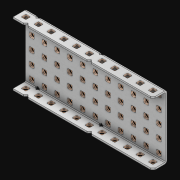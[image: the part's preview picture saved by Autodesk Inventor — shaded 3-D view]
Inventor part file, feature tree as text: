
AUTODESK INVENTOR PART (.ipt)
format: ipt  version: 2021 (Build 250183000, 183)  size: 3,133,440 bytes
history: native  units: in
note: dims shown in document units (in); Inventor stores cm internally (conversion verified against a paired STEP export)
features: extrude x78, other x77, sketch x4, thicken_offset x3, pattern_linear x3, imported_body x1
ambient origin geometry x8: Origin, YZ Plane, XZ Plane, XY Plane, X Axis, Y Axis, Z Axis, Center Point
bodies: Solid1 (feature_tree)
feature tree (166):
  thicken_offset  "Thicken1"
  thicken_offset  "Thicken2"
  thicken_offset  "Thicken3"
  pattern_linear  "Rectangular Pattern1"  Spacing1=0.001in  [1 undecoded]
  pattern_linear  "Rectangular Pattern2"  Spacing1=0.001in  [1 undecoded]
  pattern_linear  "Rectangular Pattern3"  Spacing1=0.182in  [1 undecoded]
  extrude  "Extrusion1"  Depth=0.063in TaperAngle=0.0deg
  sketch  "Sketch1"  dims[d0=0.001in]
  other  "Srf1"
  sketch  "Sketch2"  dims[d1=0.001in]
  other  "Srf2"
  sketch  "Sketch3"  dims[d2=0.001in]
  other  "Srf3"
  other  "Srf4"
  other  "Srf5"
  other  "Srf6"
  other  "Srf7"
  other  "Srf8"
  other  "Srf9"
  other  "Srf10"
  other  "Srf11"
  other  "Srf12"
  other  "Srf13"
  other  "Srf38"
  other  "Srf39"
  other  "Srf40"
  other  "Srf41"
  other  "Srf42"
  other  "Srf43"
  other  "Srf44"
  other  "Srf45"
  other  "Srf46"
  other  "Srf47"
  other  "Srf72"
  other  "Srf73"
  other  "Srf74"
  other  "Srf75"
  other  "Srf76"
  other  "Srf77"
  other  "Srf78"
  other  "Srf79"
  other  "Srf80"
  other  "Srf81"
  other  "Srf106"
  other  "Srf107"
  other  "Srf108"
  other  "Srf109"
  other  "Srf110"
  other  "Srf111"
  other  "Srf112"
  other  "Srf113"
  other  "Srf114"
  other  "Srf115"
  other  "Srf116"
  other  "Srf141"
  other  "Srf142"
  other  "Srf143"
  other  "Srf144"
  other  "Srf145"
  other  "Srf146"
  other  "Srf147"
  other  "Srf148"
  other  "Srf149"
  other  "Srf150"
  other  "Srf151"
  other  "Srf176"
  other  "Srf177"
  other  "Srf178"
  other  "Srf179"
  other  "Srf180"
  other  "Srf181"
  other  "Srf182"
  other  "Srf183"
  other  "Srf184"
  other  "Srf185"
  other  "Srf186"
  other  "Srf211"
  other  "Srf212"
  other  "Srf213"
  other  "Srf214"
  other  "Srf215"
  other  "Srf216"
  other  "Srf217"
  other  "Srf218"
  other  "Srf219"
  other  "Srf220"
  other  "Srf221"
  sketch  "Sketch4"  dims[d3=0.001in d4=0.001in d5=0.001in d6=0.182in d7=0.063in d8=0.0in d9=0.182in d10=0.063in d11=0.0in d12=0.182in d13=0.063in d14=0.0in d17=0.5in d18=4.3307in d20=0.5in d21=4.3307in d23=0.5in d24=1.9685in d26=0.5in d27=12.0in d28=0.0in]
  imported_body  "Imported1"
  extrude  "ExtrusionSrf1"  Depth=0.063in
  extrude  "ExtrusionSrf2"  Depth=0.063in TaperAngle=0.0deg
  extrude  "ExtrusionSrf3"  Depth=0.063in
  extrude  "ExtrusionSrf4"  Depth=0.063in TaperAngle=0.0deg
  extrude  "ExtrusionSrf5"  Depth=0.063in
  extrude  "ExtrusionSrf6"  Depth=0.063in
  extrude  "ExtrusionSrf7"  Depth=0.063in
  extrude  "ExtrusionSrf8"  Depth=0.063in
  extrude  "ExtrusionSrf9"  Depth=0.063in
  extrude  "ExtrusionSrf10"  Depth=0.063in
  extrude  "ExtrusionSrf11"  Depth=0.063in
  extrude  "ExtrusionSrf12"  TaperAngle=0.0deg  [1 undecoded]
  extrude  "ExtrusionSrf13"  [1 undecoded]
  extrude  "ExtrusionSrf38"  [1 undecoded]
  extrude  "ExtrusionSrf39"  [1 undecoded]
  extrude  "ExtrusionSrf40"  [1 undecoded]
  extrude  "ExtrusionSrf41"  [1 undecoded]
  extrude  "ExtrusionSrf42"  [1 undecoded]
  extrude  "ExtrusionSrf43"  [1 undecoded]
  extrude  "ExtrusionSrf44"  [1 undecoded]
  extrude  "ExtrusionSrf45"  [1 undecoded]
  extrude  "ExtrusionSrf46"  [1 undecoded]
  extrude  "ExtrusionSrf47"  [1 undecoded]
  extrude  "ExtrusionSrf72"  [1 undecoded]
  extrude  "ExtrusionSrf73"  [1 undecoded]
  extrude  "ExtrusionSrf74"  [1 undecoded]
  extrude  "ExtrusionSrf75"  [1 undecoded]
  extrude  "ExtrusionSrf76"  [1 undecoded]
  extrude  "ExtrusionSrf77"  [1 undecoded]
  extrude  "ExtrusionSrf78"  [1 undecoded]
  extrude  "ExtrusionSrf79"  [1 undecoded]
  extrude  "ExtrusionSrf80"  [1 undecoded]
  extrude  "ExtrusionSrf81"  [1 undecoded]
  extrude  "ExtrusionSrf106"  [1 undecoded]
  extrude  "ExtrusionSrf107"  [1 undecoded]
  extrude  "ExtrusionSrf108"  [1 undecoded]
  extrude  "ExtrusionSrf109"  [1 undecoded]
  extrude  "ExtrusionSrf110"  [1 undecoded]
  extrude  "ExtrusionSrf111"  [1 undecoded]
  extrude  "ExtrusionSrf112"  [1 undecoded]
  extrude  "ExtrusionSrf113"  [1 undecoded]
  extrude  "ExtrusionSrf114"  [1 undecoded]
  extrude  "ExtrusionSrf115"  [1 undecoded]
  extrude  "ExtrusionSrf116"  [1 undecoded]
  extrude  "ExtrusionSrf141"  [1 undecoded]
  extrude  "ExtrusionSrf142"  [1 undecoded]
  extrude  "ExtrusionSrf143"  [1 undecoded]
  extrude  "ExtrusionSrf144"  [1 undecoded]
  extrude  "ExtrusionSrf145"  [1 undecoded]
  extrude  "ExtrusionSrf146"  [1 undecoded]
  extrude  "ExtrusionSrf147"  [1 undecoded]
  extrude  "ExtrusionSrf148"  [1 undecoded]
  extrude  "ExtrusionSrf149"  [1 undecoded]
  extrude  "ExtrusionSrf150"  [1 undecoded]
  extrude  "ExtrusionSrf151"  [1 undecoded]
  extrude  "ExtrusionSrf176"  [1 undecoded]
  extrude  "ExtrusionSrf177"  [1 undecoded]
  extrude  "ExtrusionSrf178"  [1 undecoded]
  extrude  "ExtrusionSrf179"  [1 undecoded]
  extrude  "ExtrusionSrf180"  [1 undecoded]
  extrude  "ExtrusionSrf181"  [1 undecoded]
  extrude  "ExtrusionSrf182"  [1 undecoded]
  extrude  "ExtrusionSrf183"  [1 undecoded]
  extrude  "ExtrusionSrf184"  [1 undecoded]
  extrude  "ExtrusionSrf185"  [1 undecoded]
  extrude  "ExtrusionSrf186"  [1 undecoded]
  extrude  "ExtrusionSrf211"  [1 undecoded]
  extrude  "ExtrusionSrf212"  [1 undecoded]
  extrude  "ExtrusionSrf213"  [1 undecoded]
  extrude  "ExtrusionSrf214"  [1 undecoded]
  extrude  "ExtrusionSrf215"  [1 undecoded]
  extrude  "ExtrusionSrf216"  [1 undecoded]
  extrude  "ExtrusionSrf217"  [1 undecoded]
  extrude  "ExtrusionSrf218"  [1 undecoded]
  extrude  "ExtrusionSrf219"  [1 undecoded]
  extrude  "ExtrusionSrf220"  [1 undecoded]
  extrude  "ExtrusionSrf221"  [1 undecoded]
note: 69 required parameter values undecoded (feature->parameter linkage not recoverable at this tier; creation-order binding heuristic only, values carry confidence <= 0.55)
